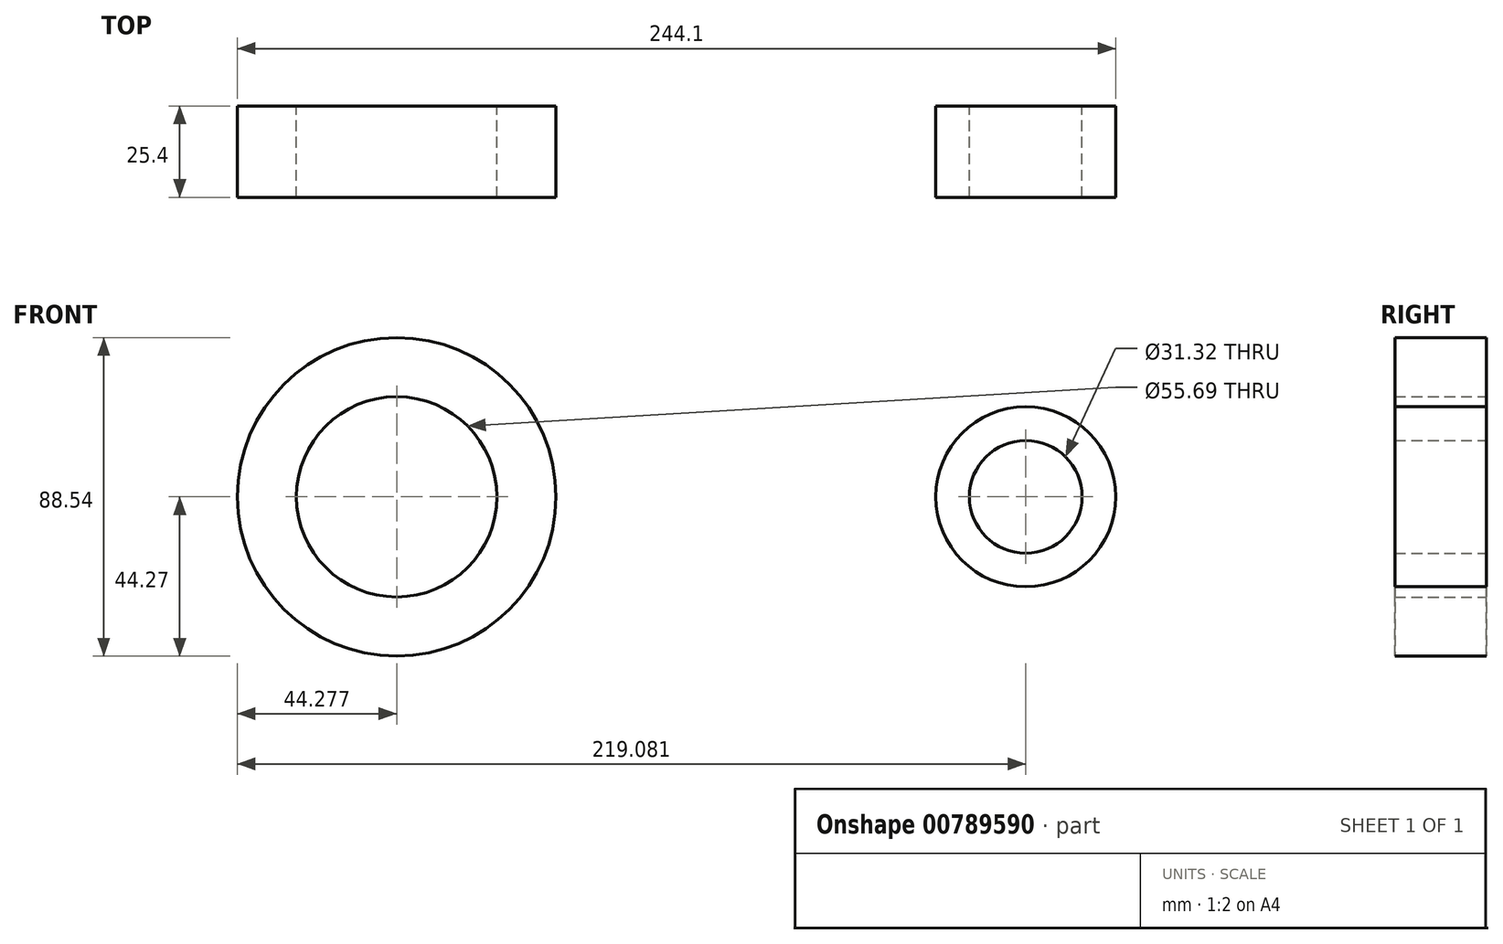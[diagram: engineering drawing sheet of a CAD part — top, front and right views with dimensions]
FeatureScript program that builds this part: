
annotation { "Feature Type Name" : "Feature", "Feature Type Description" : "" }
export const myFeature = defineFeature(function(context is Context, id is Id, definition is map)
    precondition{}
    {
        {
            var Q0;
            Q0=qCreatedBy(makeId("Front.planeOp"),FACE);
            var sketch = newSketch(context, id + "F0", { "sketchPlane" : qUnion([Q0])});
            skCircle(sketch, "E0", {"center": v(-57.83, 0) * mm, "radius": 27.85 * mm});
            skCircle(sketch, "E1", {"center": v(-57.83, 0) * mm, "radius": 44.27 * mm});
            skSolve(sketch);
        }
        {
            var Q0;
            Q0 = qSketchRegion(id + "F0", true);
            extrude(context, id + "F1", {"entities" : qUnion([Q0]), "depth" : 25.4 * mm, "offsetDistance" : 25.4 * mm});
        }
        {
            var Q0;
            Q0=qCreatedBy(makeId("Front.planeOp"),FACE);
            var sketch = newSketch(context, id + "F2", { "sketchPlane" : qUnion([Q0])});
            skCircle(sketch, "E2", {"center": v(116.97, 0) * mm, "radius": 25.01 * mm});
            skCircle(sketch, "E3", {"center": v(116.97, 0) * mm, "radius": 15.66 * mm});
            skSolve(sketch);
        }
        {
            var Q0;
            Q0 = qSketchRegion(id + "F2", true);
            extrude(context, id + "F3", {"entities" : qUnion([Q0]), "depth" : 25.4 * mm, "offsetDistance" : 25.4 * mm});
        }
        {
            var Q0;
            Q0=qCreatedBy(makeId("Front.planeOp"),FACE);
            var sketch = newSketch(context, id + "F4", { "sketchPlane" : qUnion([Q0])});
            skLineSegment(sketch, "E4", {"start": v(-58.7, 45.44) * mm, "end": v(108.27, 24.13) * mm});
            skLineSegment(sketch, "E5", {"start": v(-58.7, -45.44) * mm, "end": v(108.27, -24.57) * mm});
            skSolve(sketch);
        }
        {
            var Q0;
            Q0=sQuery(id+"F4.wireOp",EDGE,"E4");
            var Q1;
            Q1=sQuery(id+"F4.wireOp",EDGE,"E5");
            extrude(context, id + "F5", {"bodyType" : ToolBodyType.SURFACE, "operationType" : NewBodyOperationType.ADD, "surfaceEntities" : qUnion([Q0, Q1]), "depth" : 25.4 * mm, "offsetDistance" : 25.4 * mm});
        }
    });
